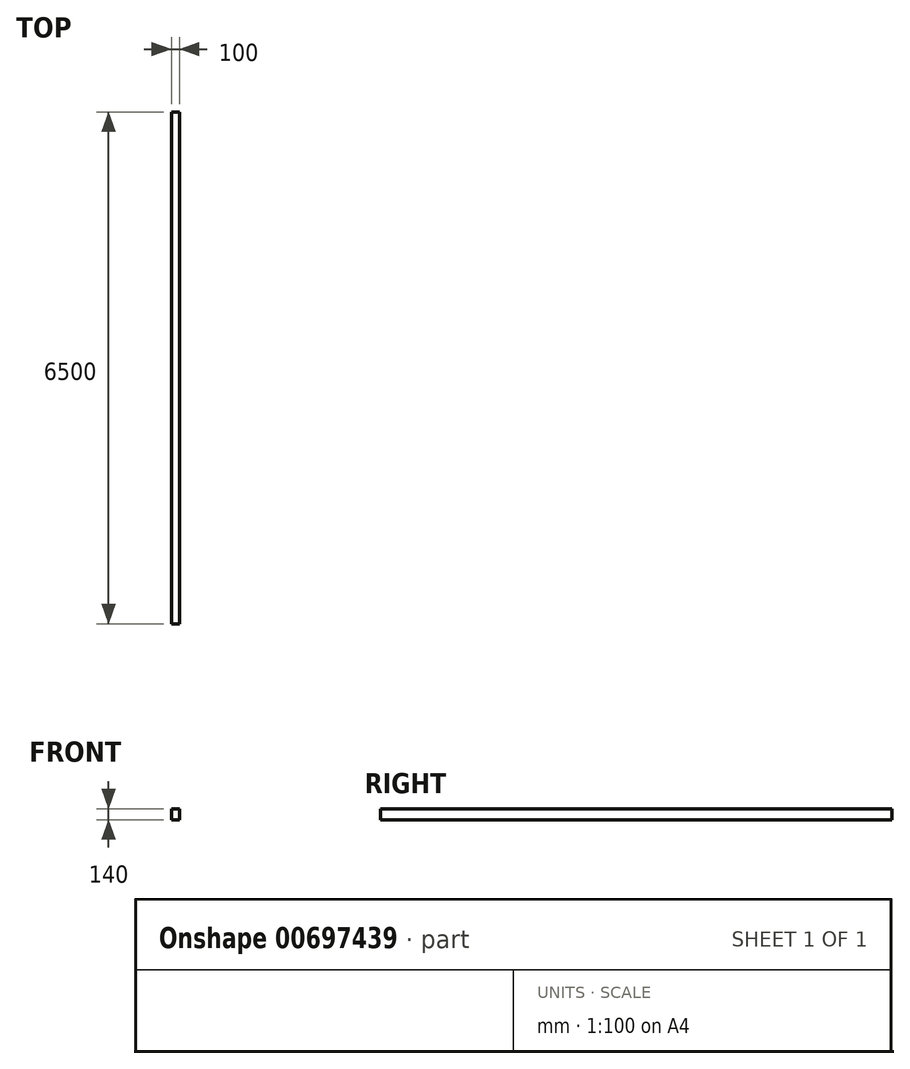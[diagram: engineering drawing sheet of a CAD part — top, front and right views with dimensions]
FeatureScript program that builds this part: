
annotation { "Feature Type Name" : "Feature", "Feature Type Description" : "" }
export const myFeature = defineFeature(function(context is Context, id is Id, definition is map)
    precondition{}
    {
        {
            var Q0;
            Q0=qCreatedBy(makeId("Front.planeOp"),FACE);
            var sketch = newSketch(context, id + "F0", { "sketchPlane" : qUnion([Q0])});
            skLineSegment(sketch, "E0.bottom", {"start": v(-93.95, -183.48) * mm, "end": v(6.05, -183.48) * mm});
            skLineSegment(sketch, "E0.top", {"start": v(-93.95, -43.48) * mm, "end": v(6.05, -43.48) * mm});
            skLineSegment(sketch, "E0.left", {"start": v(-93.95, -183.48) * mm, "end": v(-93.95, -43.48) * mm});
            skLineSegment(sketch, "E0.right", {"start": v(6.05, -183.48) * mm, "end": v(6.05, -43.48) * mm});
            skSolve(sketch);
        }
        {
            var Q0;
            Q0=makeQuery(id+"F0.imprint","IMPRINT",FACE,{"disambiguationData":[TD([[makeQuery(id+"F0.imprint","IMPRINT",EDGE,{"derivedFrom":sQuery(id+"F0.wireOp",EDGE,"E0.bottom")}),1.0]])]});
            extrude(context, id + "F1", {"entities" : qUnion([Q0]), "depth" : 6500 * mm, "offsetDistance" : 25 * mm});
        }
    });
